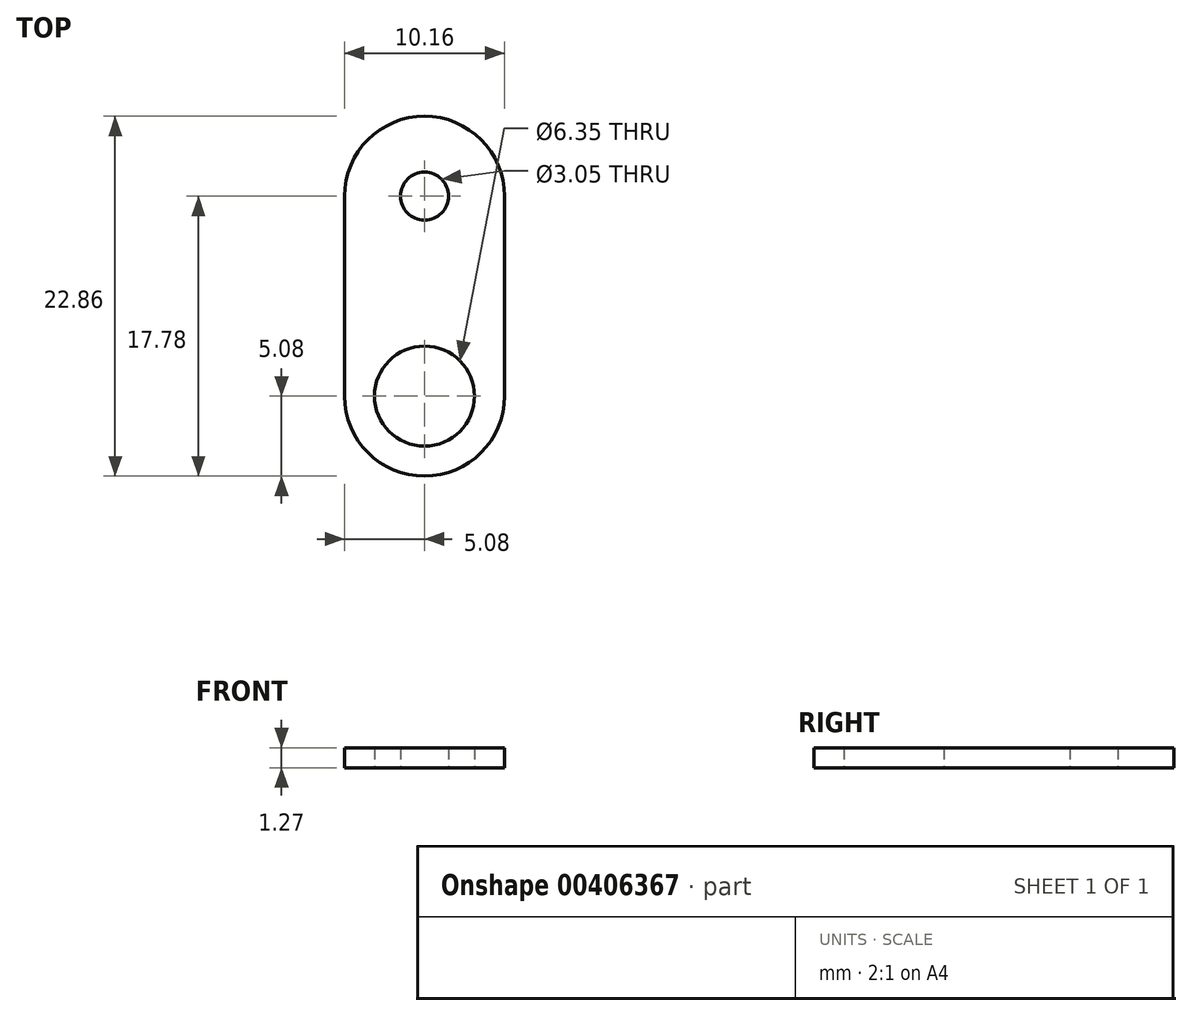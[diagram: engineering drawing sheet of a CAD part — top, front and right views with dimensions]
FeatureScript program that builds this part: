
annotation { "Feature Type Name" : "Feature", "Feature Type Description" : "" }
export const myFeature = defineFeature(function(context is Context, id is Id, definition is map)
    precondition{}
    {
        {
            var Q0;
            Q0=qCreatedBy(makeId("Top.planeOp"),FACE);
            var sketch = newSketch(context, id + "F0", { "sketchPlane" : qUnion([Q0])});
            skLineSegment(sketch, "E0", {"start": v(-5.08, 6.35) * mm, "end": v(-5.08, -6.35) * mm});
            skLineSegment(sketch, "E1", {"start": v(5.08, 6.35) * mm, "end": v(5.08, -6.35) * mm});
            skArc(sketch, "E2", {"start": v(5.08, 6.35) * mm, "mid": v(0, 11.43) * mm, "end": v(-5.08, 6.35) * mm});
            skArc(sketch, "E3", {"start": v(-5.08, -6.35) * mm, "mid": v(0, -11.43) * mm, "end": v(5.08, -6.35) * mm});
            skLineSegment(sketch, "E4", {"start": v(-12.5, 0) * mm, "end": v(11.34, 0) * mm, "construction": true});
            skCircle(sketch, "E5", {"center": v(0, -6.35) * mm, "radius": 3.18 * mm});
            skCircle(sketch, "E6", {"center": v(0, 6.35) * mm, "radius": 1.52 * mm});
            skSolve(sketch);
        }
        {
            var Q0;
            Q0 = qSketchRegion(id + "F0", true);
            extrude(context, id + "F1", {"entities" : qUnion([Q0]), "depth" : 1.27 * mm});
        }
    });
